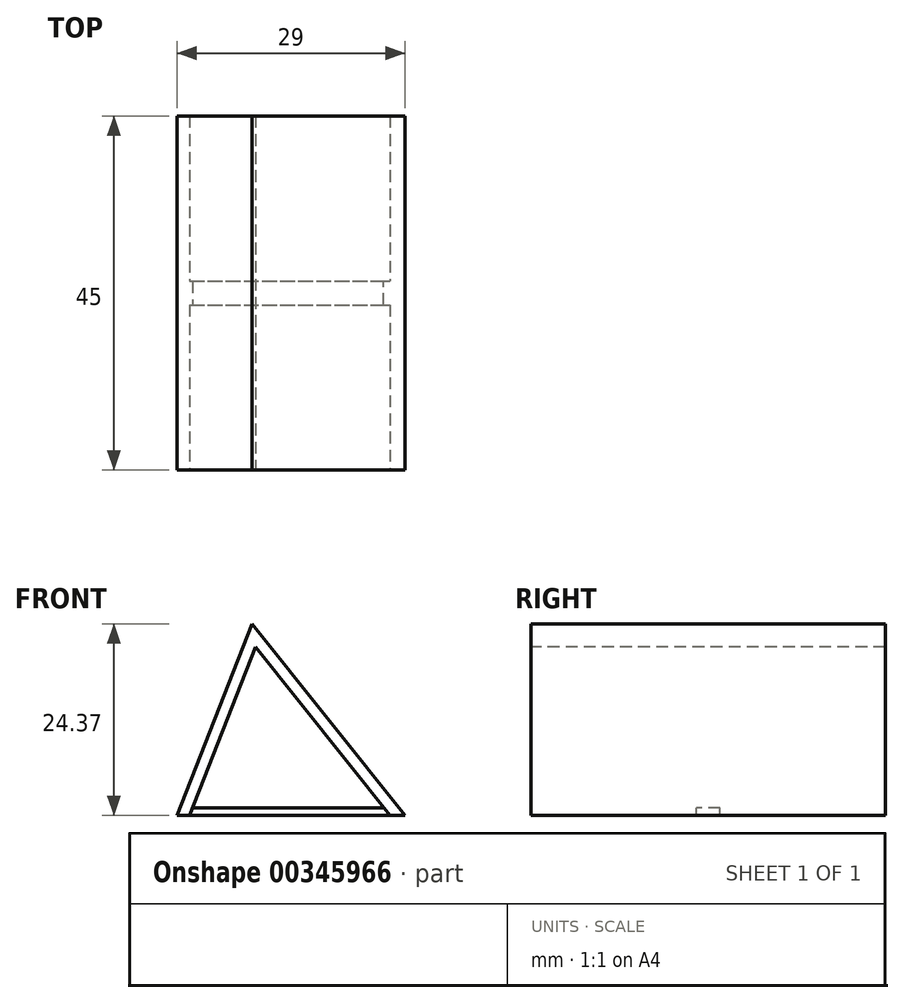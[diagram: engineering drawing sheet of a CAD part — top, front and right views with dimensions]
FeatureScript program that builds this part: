
annotation { "Feature Type Name" : "Feature", "Feature Type Description" : "" }
export const myFeature = defineFeature(function(context is Context, id is Id, definition is map)
    precondition{}
    {
        {
            var Q0;
            Q0=qCreatedBy(makeId("Front.planeOp"),FACE);
            var sketch = newSketch(context, id + "F0", { "sketchPlane" : qUnion([Q0])});
            skLineSegment(sketch, "E0", {"start": v(-10, 0) * mm, "end": v(-8.39, 0) * mm});
            skLineSegment(sketch, "E1", {"start": v(-8.39, 0) * mm, "end": v(0, 21.4) * mm});
            skLineSegment(sketch, "E2", {"start": v(0, 21.4) * mm, "end": v(17.08, 0) * mm});
            skLineSegment(sketch, "E3", {"start": v(-0.45, 24.37) * mm, "end": v(-10, 0) * mm});
            skLineSegment(sketch, "E4", {"start": v(-0.45, 24.37) * mm, "end": v(19, 0) * mm});
            skLineSegment(sketch, "E5", {"start": v(19, 0) * mm, "end": v(17.08, 0) * mm});
            skSolve(sketch);
        }
        {
            var Q0;
            Q0=makeQuery(id+"F0.imprint","IMPRINT",FACE,{"disambiguationData":[TD([[makeQuery(id+"F0.imprint","IMPRINT",EDGE,{"derivedFrom":sQuery(id+"F0.wireOp",EDGE,"E0")}),1.0]])]});
            extrude(context, id + "F1", {"entities" : qUnion([Q0]), "endBound" : BoundingType.SYMMETRIC, "oppositeDirection" : true, "depth" : 45 * mm});
        }
        {
            var Q0;
            Q0=qCreatedBy(makeId("Top.planeOp"),FACE);
            var sketch = newSketch(context, id + "F2", { "sketchPlane" : qUnion([Q0])});
            skLineSegment(sketch, "E6.left", {"start": v(19, -1.5) * mm, "end": v(19, 1.5) * mm});
            skPoint(sketch, "E6.middle", {"position": v(0, 0) * mm});
            skPoint(sketch, "E7", {"position": v(-10, -1.5) * mm});
            skPoint(sketch, "E8", {"position": v(-10, 1.5) * mm});
            skLineSegment(sketch, "E9", {"start": v(-10, -1.5) * mm, "end": v(-10, 1.5) * mm});
            skLineSegment(sketch, "E10", {"start": v(-10, -1.5) * mm, "end": v(19, -1.5) * mm});
            skLineSegment(sketch, "E11", {"start": v(-10, 1.5) * mm, "end": v(19, 1.5) * mm});
            skSolve(sketch);
        }
        {
            var Q0;
            Q0=makeQuery(id+"F2.imprint","IMPRINT",FACE,{"disambiguationData":[TD([[makeQuery(id+"F2.imprint","IMPRINT",EDGE,{"derivedFrom":sQuery(id+"F2.wireOp",EDGE,"E6.left")}),1.0]])]});
            var Q1;
            Q1=makeQuery(id+"F1.opExtrude","CAP_VERTEX",VERTEX,{"disambiguationData":[OSD([sQuery(id+"F0.wireOp",EDGE,"E1"),sQuery(id+"F0.wireOp",EDGE,"E2")])],"isStart":true});
            var Q2;
            Q2=makeQuery(id+"F1.opExtrude","SWEPT_FACE",FACE,{"disambiguationData":[OSD([sQuery(id+"F0.wireOp",EDGE,"E4")])]});
            extrude(context, id + "F3", {"entities" : qUnion([Q0]), "operationType" : NewBodyOperationType.ADD, "endBoundEntityVertex" : qUnion([Q1]), "depth" : 1 * mm});
        }
        {
            var Q0;
            {var subQ2=sQuery(id+"F2.wireOp",EDGE,"E10");Q0=makeQuery(id+"F3.boolean.opBoolean","SPLIT",FACE,{"disambiguationData":[TD([makeQuery(id+"F1.opExtrude","SWEPT_FACE",FACE,{"disambiguationData":[OSD([sQuery(id+"F0.wireOp",EDGE,"E4")])]})])],"derivedFrom":makeQuery(id+"F3.opExtrude","SWEPT_FACE",FACE,{"disambiguationData":[OSD([subQ2])]})});}
            var Q1;
            {var subQ1=sQuery(id+"F2.wireOp",EDGE,"E10");Q1=makeQuery(id+"F3.boolean.opBoolean","SPLIT",FACE,{"disambiguationData":[TD([makeQuery(id+"F1.opExtrude","SWEPT_FACE",FACE,{"disambiguationData":[OSD([sQuery(id+"F0.wireOp",EDGE,"E3")])]})])],"derivedFrom":makeQuery(id+"F3.opExtrude","SWEPT_FACE",FACE,{"disambiguationData":[OSD([subQ1])]})});}
            extrude(context, id + "F4", {"entities" : qUnion([Q0, Q1]), "operationType" : NewBodyOperationType.REMOVE, "endBound" : BoundingType.THROUGH_ALL, "oppositeDirection" : true, "depth" : 25 * mm});
        }
    });
